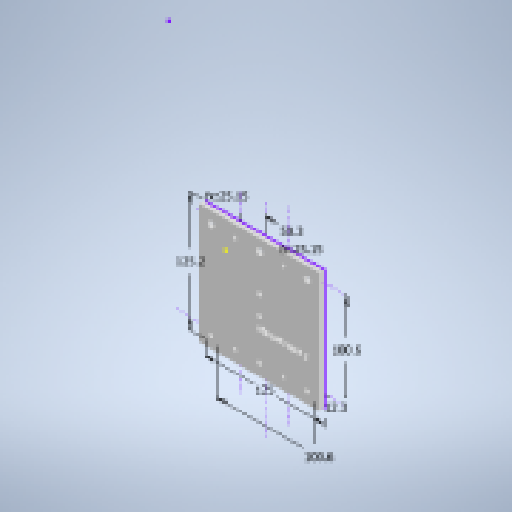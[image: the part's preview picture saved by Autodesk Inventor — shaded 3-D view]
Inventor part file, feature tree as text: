
AUTODESK INVENTOR PART (.ipt)
format: ipt  version: 2023.2 (Build 272271000, 271)  size: 465,408 bytes
history: native  units: mm
features: sketch x4, hole x4, other x3, extrude x1, reference x1
ambient origin geometry x8: Origin, YZ Plane, XZ Plane, XY Plane, X Axis, Y Axis, Z Axis, Center Point
bodies: Solid1 (feature_tree)
feature tree (13):
  sketch  "Sketch1"  dims[d0=125.0mm d1=125.2mm d6=100.6mm d11=6.0mm d12=0.0mm d48=12.3mm]
  extrude  "Extrusion1"  Depth=6.0mm
  hole  "Hole6"  [1 undecoded]
  sketch  "Sketch2"  dims[d49=100.6mm d50=50.3mm]
  sketch  "Sketch3"  dims[d51=5.1mm d52=6.0mm d53=9.2mm d54=3.0mm d55=90.0deg d56=8.0mm d57=20.594885mm]
  hole  "Hole7"  [1 undecoded]
  hole  "Hole8"  [1 undecoded]
  hole  "Hole9"  [1 undecoded]
  reference  "Reference7"
  sketch  "Sketch5"  dims[d58=7.2mm d59=6.0mm d60=12.25mm d61=3.0mm d62=90.0deg d63=8.0mm d64=20.594885mm d65=5.1mm d66=6.0mm d67=9.2mm d68=3.0mm d69=90.0deg d70=8.0mm d71=20.594885mm d72=25.15mm d73=25.15mm d74=4.2mm d75=6.0mm d76=9.2mm d77=2.0mm d78=90.0deg d79=8.0mm d80=20.594885mm d81=10.0mm d82=10.0mm]
  parser-record x1  (decoder bookkeeping rows leaked as tree rows — omitted from the tree; the rows remain in map.json)
  other  "Main Assembly.iam"
  other  "Z axis carriage small 2:1"
note: 4 required parameter values undecoded (feature->parameter linkage not recoverable at this tier; creation-order binding heuristic only, values carry confidence <= 0.55)
note: 1 file-system path scrubbed to <path> (originals preserved in map.json)
